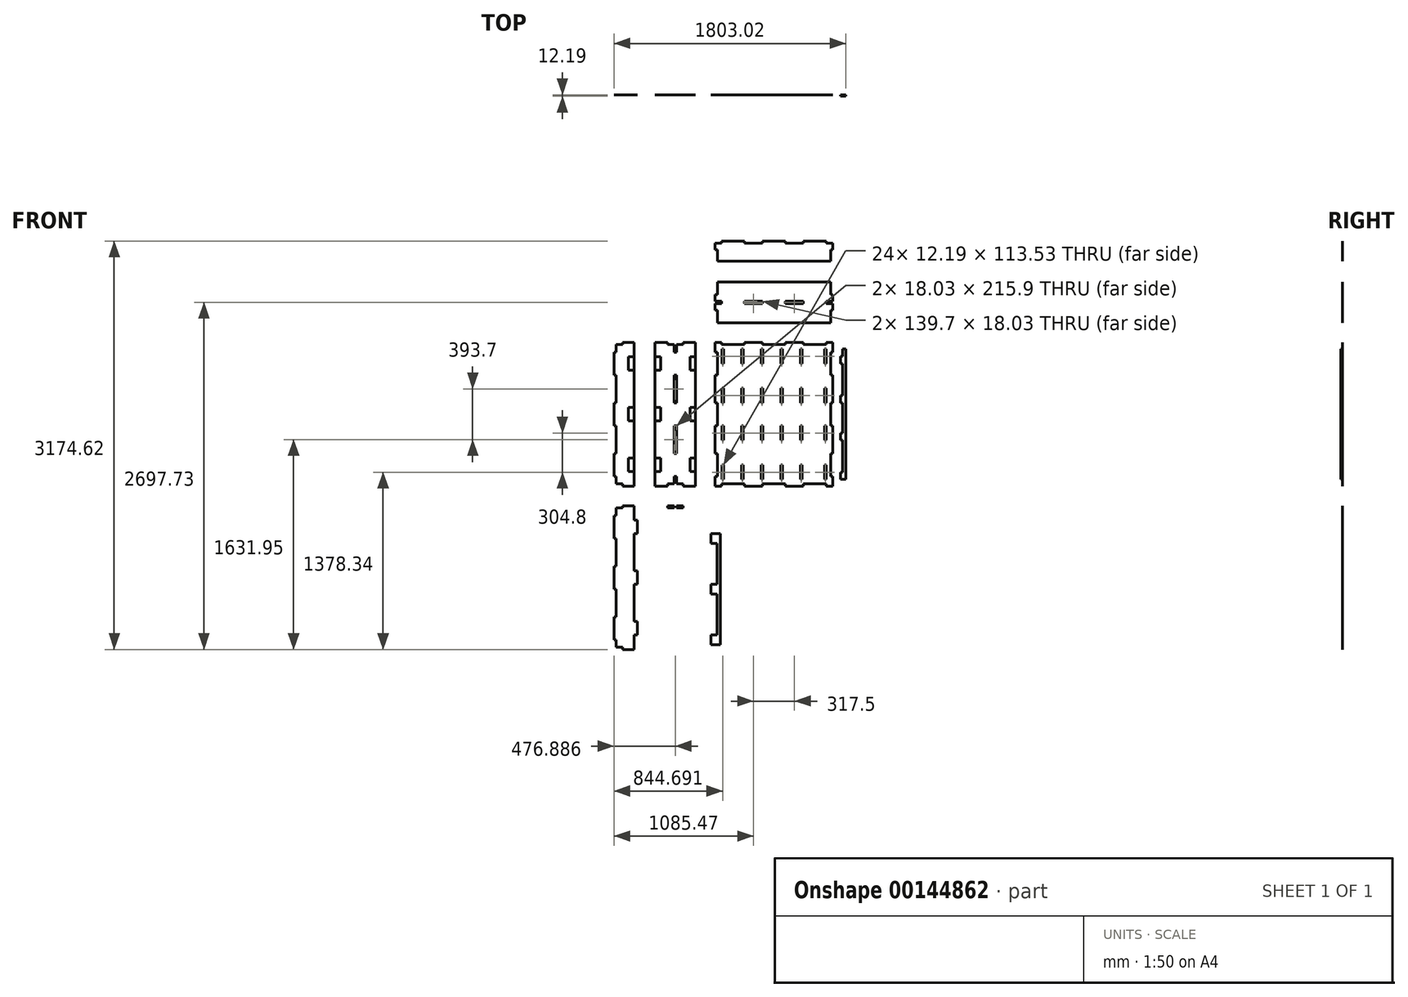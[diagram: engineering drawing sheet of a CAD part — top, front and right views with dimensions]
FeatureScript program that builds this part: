
annotation { "Feature Type Name" : "Feature", "Feature Type Description" : "" }
export const myFeature = defineFeature(function(context is Context, id is Id, definition is map)
    precondition{}
    {
        {
            assignVariable(context, id + "F0", {"name" : "ply34", "anyValue" : 0.71});
        }
        {
            var Q0;
            Q0=qCreatedBy(makeId("Front.planeOp"),FACE);
            var sketch = newSketch(context, id + "F1", { "sketchPlane" : qUnion([Q0])});
            skLineSegment(sketch, "E0.bottom", {"start": v(-457.2, 558.8) * mm, "end": v(457.2, 558.8) * mm});
            skLineSegment(sketch, "E0.top", {"start": v(-457.2, -558.8) * mm, "end": v(457.2, -558.8) * mm});
            skLineSegment(sketch, "E0.left", {"start": v(-457.2, 558.8) * mm, "end": v(-457.2, -558.8) * mm});
            skLineSegment(sketch, "E0.right", {"start": v(457.2, 558.8) * mm, "end": v(457.2, -558.8) * mm});
            skPoint(sketch, "E0.middle", {"position": v(0, 0) * mm});
            skLineSegment(sketch, "E1.bottom", {"start": v(-457.2, 482.6) * mm, "end": v(-439.17, 482.6) * mm});
            skLineSegment(sketch, "E1.top", {"start": v(-457.2, 304.8) * mm, "end": v(-439.17, 304.8) * mm});
            skLineSegment(sketch, "E1.left", {"start": v(-457.2, 482.6) * mm, "end": v(-457.2, 304.8) * mm});
            skLineSegment(sketch, "E1.right", {"start": v(-439.17, 482.6) * mm, "end": v(-439.17, 304.8) * mm});
            skLineSegment(sketch, "E2.bottom", {"start": v(-457.2, 88.9) * mm, "end": v(-439.17, 88.9) * mm});
            skLineSegment(sketch, "E2.top", {"start": v(-457.2, -88.9) * mm, "end": v(-439.17, -88.9) * mm});
            skLineSegment(sketch, "E2.left", {"start": v(-457.2, 88.9) * mm, "end": v(-457.2, -88.9) * mm});
            skLineSegment(sketch, "E2.right", {"start": v(-439.17, 88.9) * mm, "end": v(-439.17, -88.9) * mm});
            skPoint(sketch, "E3", {"position": v(-439.17, 0) * mm});
            skLineSegment(sketch, "E4", {"start": v(-457.2, 0) * mm, "end": v(457.2, 0) * mm, "construction": true});
            skLineSegment(sketch, "E5", {"start": v(0, 558.8) * mm, "end": v(0, -558.8) * mm, "construction": true});
            skLineSegment(sketch, "E6.MirrorCS", {"start": v(-457.2, -482.6) * mm, "end": v(-439.17, -482.6) * mm});
            skLineSegment(sketch, "E7.MirrorCS", {"start": v(-457.2, -304.8) * mm, "end": v(-439.17, -304.8) * mm});
            skLineSegment(sketch, "E8.MirrorCS", {"start": v(-457.2, -482.6) * mm, "end": v(-457.2, -304.8) * mm});
            skLineSegment(sketch, "E9.MirrorCS", {"start": v(-439.17, -482.6) * mm, "end": v(-439.17, -304.8) * mm});
            skLineSegment(sketch, "E10.MirrorCS", {"start": v(457.2, -88.9) * mm, "end": v(439.17, -88.9) * mm});
            skLineSegment(sketch, "E11.MirrorCS", {"start": v(457.2, 304.8) * mm, "end": v(439.17, 304.8) * mm});
            skLineSegment(sketch, "E12.MirrorCS", {"start": v(457.2, 482.6) * mm, "end": v(439.17, 482.6) * mm});
            skLineSegment(sketch, "E13.MirrorCS", {"start": v(457.2, 88.9) * mm, "end": v(439.17, 88.9) * mm});
            skLineSegment(sketch, "E14.MirrorCS", {"start": v(457.2, -304.8) * mm, "end": v(439.17, -304.8) * mm});
            skLineSegment(sketch, "E15.MirrorCS", {"start": v(457.2, -482.6) * mm, "end": v(439.17, -482.6) * mm});
            skLineSegment(sketch, "E16.MirrorCS", {"start": v(439.17, 88.9) * mm, "end": v(439.17, -88.9) * mm});
            skLineSegment(sketch, "E17.MirrorCS", {"start": v(457.2, 88.9) * mm, "end": v(457.2, -88.9) * mm});
            skLineSegment(sketch, "E18.MirrorCS", {"start": v(457.2, -482.6) * mm, "end": v(457.2, -304.8) * mm});
            skLineSegment(sketch, "E19.MirrorCS", {"start": v(439.17, -482.6) * mm, "end": v(439.17, -304.8) * mm});
            skLineSegment(sketch, "E20.MirrorCS", {"start": v(457.2, 482.6) * mm, "end": v(457.2, 304.8) * mm});
            skPoint(sketch, "E21.MirrorP", {"position": v(439.17, 0) * mm});
            skLineSegment(sketch, "E22.MirrorCS", {"start": v(439.17, 482.6) * mm, "end": v(439.17, 304.8) * mm});
            skLineSegment(sketch, "E23.bottom", {"start": v(-406.4, 558.8) * mm, "end": v(-228.6, 558.8) * mm});
            skLineSegment(sketch, "E23.top", {"start": v(-406.4, 540.77) * mm, "end": v(-228.6, 540.77) * mm});
            skLineSegment(sketch, "E23.left", {"start": v(-406.4, 558.8) * mm, "end": v(-406.4, 540.77) * mm});
            skLineSegment(sketch, "E23.right", {"start": v(-228.6, 558.8) * mm, "end": v(-228.6, 540.77) * mm});
            skLineSegment(sketch, "E24.bottom", {"start": v(-88.9, 558.8) * mm, "end": v(88.9, 558.8) * mm});
            skLineSegment(sketch, "E24.top", {"start": v(-88.9, 540.77) * mm, "end": v(88.9, 540.77) * mm});
            skLineSegment(sketch, "E24.left", {"start": v(-88.9, 558.8) * mm, "end": v(-88.9, 540.77) * mm});
            skLineSegment(sketch, "E24.right", {"start": v(88.9, 558.8) * mm, "end": v(88.9, 540.77) * mm});
            skPoint(sketch, "E25", {"position": v(0, 558.8) * mm});
            skLineSegment(sketch, "E26.MirrorCS", {"start": v(228.6, 558.8) * mm, "end": v(228.6, 540.77) * mm});
            skLineSegment(sketch, "E27.MirrorCS", {"start": v(406.4, 558.8) * mm, "end": v(406.4, 540.77) * mm});
            skLineSegment(sketch, "E28.MirrorCS", {"start": v(406.4, 540.77) * mm, "end": v(228.6, 540.77) * mm});
            skLineSegment(sketch, "E29.MirrorCS", {"start": v(406.4, 558.8) * mm, "end": v(228.6, 558.8) * mm});
            skLineSegment(sketch, "E30.MirrorCS", {"start": v(-88.9, -558.8) * mm, "end": v(88.9, -558.8) * mm});
            skLineSegment(sketch, "E31.MirrorCS", {"start": v(228.6, -558.8) * mm, "end": v(228.6, -540.77) * mm});
            skLineSegment(sketch, "E32.MirrorCS", {"start": v(-228.6, -558.8) * mm, "end": v(-228.6, -540.77) * mm});
            skLineSegment(sketch, "E33.MirrorCS", {"start": v(88.9, -558.8) * mm, "end": v(88.9, -540.77) * mm});
            skLineSegment(sketch, "E34.MirrorCS", {"start": v(-406.4, -558.8) * mm, "end": v(-406.4, -540.77) * mm});
            skLineSegment(sketch, "E35.MirrorCS", {"start": v(-88.9, -558.8) * mm, "end": v(-88.9, -540.77) * mm});
            skLineSegment(sketch, "E36.MirrorCS", {"start": v(406.4, -558.8) * mm, "end": v(406.4, -540.77) * mm});
            skLineSegment(sketch, "E37.MirrorCS", {"start": v(-406.4, -558.8) * mm, "end": v(-228.6, -558.8) * mm});
            skLineSegment(sketch, "E38.MirrorCS", {"start": v(-88.9, -540.77) * mm, "end": v(88.9, -540.77) * mm});
            skLineSegment(sketch, "E39.MirrorCS", {"start": v(-406.4, -540.77) * mm, "end": v(-228.6, -540.77) * mm});
            skLineSegment(sketch, "E40.MirrorCS", {"start": v(406.4, -558.8) * mm, "end": v(228.6, -558.8) * mm});
            skLineSegment(sketch, "E41.MirrorCS", {"start": v(406.4, -540.77) * mm, "end": v(228.6, -540.77) * mm});
            skPoint(sketch, "E42.MirrorP", {"position": v(0, -558.8) * mm});
            skLineSegment(sketch, "E43.bottom", {"start": v(-609.6, -558.8) * mm, "end": v(-925.07, -558.8) * mm});
            skLineSegment(sketch, "E43.top", {"start": v(-609.6, 558.8) * mm, "end": v(-925.07, 558.8) * mm});
            skLineSegment(sketch, "E43.left", {"start": v(-609.6, -558.8) * mm, "end": v(-609.6, 558.8) * mm});
            skLineSegment(sketch, "E43.right", {"start": v(-925.07, -558.8) * mm, "end": v(-925.07, 558.8) * mm});
            skLineSegment(sketch, "E44.bottom", {"start": v(-776.35, 558.8) * mm, "end": v(-758.32, 558.8) * mm});
            skLineSegment(sketch, "E44.top", {"start": v(-776.35, 482.6) * mm, "end": v(-758.32, 482.6) * mm});
            skLineSegment(sketch, "E44.left", {"start": v(-776.35, 558.8) * mm, "end": v(-776.35, 482.6) * mm});
            skLineSegment(sketch, "E44.right", {"start": v(-758.32, 558.8) * mm, "end": v(-758.32, 482.6) * mm});
            skPoint(sketch, "E45", {"position": v(-767.33, 558.8) * mm});
            skLineSegment(sketch, "E46.bottom", {"start": v(-776.35, 304.8) * mm, "end": v(-758.32, 304.8) * mm});
            skLineSegment(sketch, "E46.top", {"start": v(-776.35, 88.9) * mm, "end": v(-758.32, 88.9) * mm});
            skLineSegment(sketch, "E46.left", {"start": v(-776.35, 304.8) * mm, "end": v(-776.35, 88.9) * mm});
            skLineSegment(sketch, "E46.right", {"start": v(-758.32, 304.8) * mm, "end": v(-758.32, 88.9) * mm});
            skLineSegment(sketch, "E47.bottom", {"start": v(-776.35, -88.9) * mm, "end": v(-758.32, -88.9) * mm});
            skLineSegment(sketch, "E47.top", {"start": v(-776.35, -304.8) * mm, "end": v(-758.32, -304.8) * mm});
            skLineSegment(sketch, "E47.left", {"start": v(-776.35, -88.9) * mm, "end": v(-776.35, -304.8) * mm});
            skLineSegment(sketch, "E47.right", {"start": v(-758.32, -88.9) * mm, "end": v(-758.32, -304.8) * mm});
            skLineSegment(sketch, "E48.bottom", {"start": v(-776.35, -482.6) * mm, "end": v(-758.32, -482.6) * mm});
            skLineSegment(sketch, "E48.top", {"start": v(-776.35, -558.8) * mm, "end": v(-758.32, -558.8) * mm});
            skLineSegment(sketch, "E48.left", {"start": v(-776.35, -482.6) * mm, "end": v(-776.35, -558.8) * mm});
            skLineSegment(sketch, "E48.right", {"start": v(-758.32, -482.6) * mm, "end": v(-758.32, -558.8) * mm});
            skLineSegment(sketch, "E49.bottom", {"start": v(-776.35, 558.8) * mm, "end": v(-827.15, 558.8) * mm});
            skLineSegment(sketch, "E49.top", {"start": v(-776.35, 540.77) * mm, "end": v(-827.15, 540.77) * mm});
            skLineSegment(sketch, "E49.left", {"start": v(-776.35, 558.8) * mm, "end": v(-776.35, 540.77) * mm});
            skLineSegment(sketch, "E49.right", {"start": v(-827.15, 558.8) * mm, "end": v(-827.15, 540.77) * mm});
            skLineSegment(sketch, "E50.bottom", {"start": v(-758.32, 558.8) * mm, "end": v(-707.52, 558.8) * mm});
            skLineSegment(sketch, "E50.top", {"start": v(-758.32, 540.77) * mm, "end": v(-707.52, 540.77) * mm});
            skLineSegment(sketch, "E50.left", {"start": v(-758.32, 558.8) * mm, "end": v(-758.32, 540.77) * mm});
            skLineSegment(sketch, "E50.right", {"start": v(-707.52, 558.8) * mm, "end": v(-707.52, 540.77) * mm});
            skLineSegment(sketch, "E51.MirrorCS", {"start": v(-758.32, -540.77) * mm, "end": v(-707.52, -540.77) * mm});
            skLineSegment(sketch, "E52.MirrorCS", {"start": v(-758.32, -558.8) * mm, "end": v(-707.52, -558.8) * mm});
            skLineSegment(sketch, "E53.MirrorCS", {"start": v(-758.32, -558.8) * mm, "end": v(-758.32, -540.77) * mm});
            skLineSegment(sketch, "E54.MirrorCS", {"start": v(-827.15, -558.8) * mm, "end": v(-827.15, -540.77) * mm});
            skLineSegment(sketch, "E55.MirrorCS", {"start": v(-776.35, -540.77) * mm, "end": v(-827.15, -540.77) * mm});
            skPoint(sketch, "E56.MirrorP", {"position": v(-767.33, -558.8) * mm});
            skLineSegment(sketch, "E57.MirrorCS", {"start": v(-776.35, -558.8) * mm, "end": v(-776.35, -540.77) * mm});
            skLineSegment(sketch, "E58.MirrorCS", {"start": v(-776.35, -558.8) * mm, "end": v(-827.15, -558.8) * mm});
            skLineSegment(sketch, "E59.MirrorCS", {"start": v(-707.52, -558.8) * mm, "end": v(-707.52, -540.77) * mm});
            skLineSegment(sketch, "E60.bottom", {"start": v(-439.17, 1026.67) * mm, "end": v(439.17, 1026.67) * mm});
            skLineSegment(sketch, "E60.top", {"start": v(-439.17, 711.2) * mm, "end": v(439.17, 711.2) * mm});
            skLineSegment(sketch, "E60.left", {"start": v(-439.17, 1026.67) * mm, "end": v(-439.17, 711.2) * mm});
            skLineSegment(sketch, "E60.right", {"start": v(439.17, 1026.67) * mm, "end": v(439.17, 711.2) * mm});
            skLineSegment(sketch, "E61.bottom", {"start": v(-439.17, 877.95) * mm, "end": v(-457.2, 877.95) * mm});
            skLineSegment(sketch, "E61.top", {"start": v(-439.17, 928.75) * mm, "end": v(-457.2, 928.75) * mm});
            skLineSegment(sketch, "E61.left", {"start": v(-439.17, 877.95) * mm, "end": v(-439.17, 928.75) * mm});
            skLineSegment(sketch, "E61.right", {"start": v(-457.2, 877.95) * mm, "end": v(-457.2, 928.75) * mm});
            skLineSegment(sketch, "E62.bottom", {"start": v(-439.17, 859.92) * mm, "end": v(-457.2, 859.92) * mm});
            skLineSegment(sketch, "E62.top", {"start": v(-439.17, 809.12) * mm, "end": v(-457.2, 809.12) * mm});
            skLineSegment(sketch, "E62.left", {"start": v(-439.17, 859.92) * mm, "end": v(-439.17, 809.12) * mm});
            skLineSegment(sketch, "E62.right", {"start": v(-457.2, 859.92) * mm, "end": v(-457.2, 809.12) * mm});
            skLineSegment(sketch, "E63", {"start": v(-448.18, 877.95) * mm, "end": v(-448.18, 859.92) * mm, "construction": true});
            skPoint(sketch, "E64", {"position": v(-448.18, 868.93) * mm});
            skPoint(sketch, "E65", {"position": v(-439.17, 868.93) * mm});
            skLineSegment(sketch, "E66.bottom", {"start": v(-439.17, 877.95) * mm, "end": v(-406.4, 877.95) * mm});
            skLineSegment(sketch, "E66.top", {"start": v(-439.17, 859.92) * mm, "end": v(-406.4, 859.92) * mm});
            skLineSegment(sketch, "E66.left", {"start": v(-439.17, 877.95) * mm, "end": v(-439.17, 859.92) * mm});
            skLineSegment(sketch, "E66.right", {"start": v(-406.4, 877.95) * mm, "end": v(-406.4, 859.92) * mm});
            skLineSegment(sketch, "E67.bottom", {"start": v(-228.6, 877.95) * mm, "end": v(-88.9, 877.95) * mm});
            skLineSegment(sketch, "E67.top", {"start": v(-228.6, 859.92) * mm, "end": v(-88.9, 859.92) * mm});
            skLineSegment(sketch, "E67.left", {"start": v(-228.6, 877.95) * mm, "end": v(-228.6, 859.92) * mm});
            skLineSegment(sketch, "E67.right", {"start": v(-88.9, 877.95) * mm, "end": v(-88.9, 859.92) * mm});
            skLineSegment(sketch, "E68.bottom", {"start": v(88.9, 877.95) * mm, "end": v(228.6, 877.95) * mm});
            skLineSegment(sketch, "E68.top", {"start": v(88.9, 859.92) * mm, "end": v(228.6, 859.92) * mm});
            skLineSegment(sketch, "E68.left", {"start": v(88.9, 877.95) * mm, "end": v(88.9, 859.92) * mm});
            skLineSegment(sketch, "E68.right", {"start": v(228.6, 877.95) * mm, "end": v(228.6, 859.92) * mm});
            skLineSegment(sketch, "E69.MirrorCS", {"start": v(439.17, 877.95) * mm, "end": v(439.17, 859.92) * mm});
            skLineSegment(sketch, "E70.MirrorCS", {"start": v(439.17, 877.95) * mm, "end": v(457.2, 877.95) * mm});
            skLineSegment(sketch, "E71.MirrorCS", {"start": v(406.4, 877.95) * mm, "end": v(406.4, 859.92) * mm});
            skLineSegment(sketch, "E72.MirrorCS", {"start": v(439.17, 928.75) * mm, "end": v(457.2, 928.75) * mm});
            skLineSegment(sketch, "E73.MirrorCS", {"start": v(448.18, 877.95) * mm, "end": v(448.18, 859.92) * mm, "construction": true});
            skLineSegment(sketch, "E74.MirrorCS", {"start": v(439.17, 809.12) * mm, "end": v(457.2, 809.12) * mm});
            skLineSegment(sketch, "E75.MirrorCS", {"start": v(439.17, 859.92) * mm, "end": v(457.2, 859.92) * mm});
            skLineSegment(sketch, "E76.MirrorCS", {"start": v(439.17, 877.95) * mm, "end": v(406.4, 877.95) * mm});
            skLineSegment(sketch, "E77.MirrorCS", {"start": v(439.17, 859.92) * mm, "end": v(406.4, 859.92) * mm});
            skLineSegment(sketch, "E78.MirrorCS", {"start": v(439.17, 877.95) * mm, "end": v(439.17, 928.75) * mm});
            skLineSegment(sketch, "E79.MirrorCS", {"start": v(439.17, 859.92) * mm, "end": v(439.17, 809.12) * mm});
            skLineSegment(sketch, "E80.MirrorCS", {"start": v(457.2, 877.95) * mm, "end": v(457.2, 928.75) * mm});
            skPoint(sketch, "E81.MirrorP", {"position": v(439.17, 868.93) * mm});
            skLineSegment(sketch, "E82.MirrorCS", {"start": v(457.2, 859.92) * mm, "end": v(457.2, 809.12) * mm});
            skPoint(sketch, "E83.MirrorP", {"position": v(448.18, 868.93) * mm});
            skLineSegment(sketch, "E84", {"start": v(-767.33, -558.8) * mm, "end": v(-767.33, 558.8) * mm, "construction": true});
            skLineSegment(sketch, "E85", {"start": v(439.17, 1102.87) * mm, "end": v(-439.17, 1102.87) * mm, "construction": true});
            skLineSegment(sketch, "E86.MirrorCS", {"start": v(228.6, 1327.78) * mm, "end": v(228.6, 1345.82) * mm});
            skLineSegment(sketch, "E87.MirrorCS", {"start": v(-228.6, 1327.78) * mm, "end": v(-228.6, 1345.82) * mm});
            skLineSegment(sketch, "E88.MirrorCS", {"start": v(-88.9, 1327.78) * mm, "end": v(-88.9, 1345.82) * mm});
            skLineSegment(sketch, "E89.MirrorCS", {"start": v(88.9, 1327.78) * mm, "end": v(88.9, 1345.82) * mm});
            skLineSegment(sketch, "E90.MirrorCS", {"start": v(-228.6, 1345.82) * mm, "end": v(-88.9, 1345.82) * mm});
            skLineSegment(sketch, "E91.MirrorCS", {"start": v(-228.6, 1327.78) * mm, "end": v(-88.9, 1327.78) * mm});
            skLineSegment(sketch, "E92.MirrorCS", {"start": v(88.9, 1345.82) * mm, "end": v(228.6, 1345.82) * mm});
            skLineSegment(sketch, "E93.MirrorCS", {"start": v(88.9, 1327.78) * mm, "end": v(228.6, 1327.78) * mm});
            skLineSegment(sketch, "E94.MirrorCS", {"start": v(439.17, 1276.98) * mm, "end": v(457.2, 1276.98) * mm});
            skLineSegment(sketch, "E95.MirrorCS", {"start": v(457.2, 1327.78) * mm, "end": v(457.2, 1276.98) * mm});
            skLineSegment(sketch, "E96.MirrorCS", {"start": v(439.17, 1327.78) * mm, "end": v(457.2, 1327.78) * mm});
            skLineSegment(sketch, "E97.MirrorCS", {"start": v(439.17, 1327.78) * mm, "end": v(406.4, 1327.78) * mm});
            skLineSegment(sketch, "E98.MirrorCS", {"start": v(406.4, 1327.78) * mm, "end": v(406.4, 1345.82) * mm});
            skLineSegment(sketch, "E99.MirrorCS", {"start": v(439.17, 1345.82) * mm, "end": v(406.4, 1345.82) * mm});
            skLineSegment(sketch, "E100.MirrorCS", {"start": v(-439.17, 1276.98) * mm, "end": v(-457.2, 1276.98) * mm});
            skLineSegment(sketch, "E101.MirrorCS", {"start": v(-457.2, 1327.78) * mm, "end": v(-457.2, 1276.98) * mm});
            skLineSegment(sketch, "E102.MirrorCS", {"start": v(-439.17, 1327.78) * mm, "end": v(-457.2, 1327.78) * mm});
            skLineSegment(sketch, "E103.MirrorCS", {"start": v(-439.17, 1327.78) * mm, "end": v(-406.4, 1327.78) * mm});
            skLineSegment(sketch, "E104.MirrorCS", {"start": v(-406.4, 1327.78) * mm, "end": v(-406.4, 1345.82) * mm});
            skLineSegment(sketch, "E105.MirrorCS", {"start": v(-439.17, 1345.82) * mm, "end": v(-406.4, 1345.82) * mm});
            skLineSegment(sketch, "E106", {"start": v(-406.4, 1345.82) * mm, "end": v(-228.6, 1345.82) * mm});
            skLineSegment(sketch, "E107", {"start": v(-88.9, 1345.82) * mm, "end": v(88.9, 1345.82) * mm});
            skLineSegment(sketch, "E108", {"start": v(228.6, 1345.82) * mm, "end": v(406.4, 1345.82) * mm});
            skLineSegment(sketch, "E109.bottom", {"start": v(-609.6, 52.07) * mm, "end": v(-653.31, 52.07) * mm});
            skLineSegment(sketch, "E109.top", {"start": v(-609.6, -52.07) * mm, "end": v(-653.31, -52.07) * mm});
            skLineSegment(sketch, "E109.left", {"start": v(-609.6, 52.07) * mm, "end": v(-609.6, -52.07) * mm});
            skLineSegment(sketch, "E109.right", {"start": v(-653.31, 52.07) * mm, "end": v(-653.31, -52.07) * mm});
            skPoint(sketch, "E110", {"position": v(-609.6, 0) * mm});
            skLineSegment(sketch, "E111", {"start": v(-758.32, 482.6) * mm, "end": v(-758.32, 304.8) * mm, "construction": true});
            skLineSegment(sketch, "E112.bottom", {"start": v(-653.31, 341.63) * mm, "end": v(-609.6, 341.63) * mm});
            skLineSegment(sketch, "E112.top", {"start": v(-653.31, 445.77) * mm, "end": v(-609.6, 445.77) * mm});
            skLineSegment(sketch, "E112.left", {"start": v(-653.31, 341.63) * mm, "end": v(-653.31, 445.77) * mm});
            skLineSegment(sketch, "E112.right", {"start": v(-609.6, 341.63) * mm, "end": v(-609.6, 445.77) * mm});
            skPoint(sketch, "E112.middle", {"position": v(-631.46, 393.7) * mm});
            skPoint(sketch, "E112.middle.positionSnap0", {"position": v(-631.46, 52.07) * mm});
            skPoint(sketch, "E112.middle.positionSnap1", {"position": v(-758.32, 393.7) * mm});
            skPoint(sketch, "E112.centerSnap0", {"position": v(-631.46, 52.07) * mm});
            skPoint(sketch, "E112.centerSnap1", {"position": v(-758.32, 393.7) * mm});
            skLineSegment(sketch, "E113.MirrorCS", {"start": v(-653.31, -341.63) * mm, "end": v(-609.6, -341.63) * mm});
            skLineSegment(sketch, "E114.MirrorCS", {"start": v(-653.31, -445.77) * mm, "end": v(-609.6, -445.77) * mm});
            skLineSegment(sketch, "E115.MirrorCS", {"start": v(-653.31, -341.63) * mm, "end": v(-653.31, -445.77) * mm});
            skPoint(sketch, "E116.MirrorP", {"position": v(-631.46, -393.7) * mm});
            skLineSegment(sketch, "E117.MirrorCS", {"start": v(-609.6, -341.63) * mm, "end": v(-609.6, -445.77) * mm});
            skLineSegment(sketch, "E118.MirrorCS", {"start": v(-881.35, -445.77) * mm, "end": v(-925.07, -445.77) * mm});
            skLineSegment(sketch, "E119.MirrorCS", {"start": v(-881.35, -341.63) * mm, "end": v(-925.07, -341.63) * mm});
            skLineSegment(sketch, "E120.MirrorCS", {"start": v(-881.35, 445.77) * mm, "end": v(-925.07, 445.77) * mm});
            skLineSegment(sketch, "E121.MirrorCS", {"start": v(-881.35, 341.63) * mm, "end": v(-925.07, 341.63) * mm});
            skLineSegment(sketch, "E122.MirrorCS", {"start": v(-925.07, -52.07) * mm, "end": v(-881.35, -52.07) * mm});
            skLineSegment(sketch, "E123.MirrorCS", {"start": v(-925.07, 52.07) * mm, "end": v(-881.35, 52.07) * mm});
            skLineSegment(sketch, "E124.MirrorCS", {"start": v(-925.07, -341.63) * mm, "end": v(-925.07, -445.77) * mm});
            skPoint(sketch, "E125.MirrorP", {"position": v(-903.21, 52.07) * mm});
            skLineSegment(sketch, "E126.MirrorCS", {"start": v(-881.35, -341.63) * mm, "end": v(-881.35, -445.77) * mm});
            skLineSegment(sketch, "E127.MirrorCS", {"start": v(-925.07, 341.63) * mm, "end": v(-925.07, 445.77) * mm});
            skLineSegment(sketch, "E128.MirrorCS", {"start": v(-881.35, 341.63) * mm, "end": v(-881.35, 445.77) * mm});
            skLineSegment(sketch, "E129.MirrorCS", {"start": v(-925.07, 52.07) * mm, "end": v(-925.07, -52.07) * mm});
            skLineSegment(sketch, "E130.MirrorCS", {"start": v(-881.35, 52.07) * mm, "end": v(-881.35, -52.07) * mm});
            skPoint(sketch, "E131.MirrorP", {"position": v(-903.21, 393.7) * mm});
            skPoint(sketch, "E132.MirrorP", {"position": v(-925.07, 0) * mm});
            skPoint(sketch, "E133.MirrorP", {"position": v(-903.21, -393.7) * mm});
            skLineSegment(sketch, "E134.bottom", {"start": v(-405.63, 507.23) * mm, "end": v(405.63, 507.23) * mm, "construction": true});
            skLineSegment(sketch, "E134.top", {"start": v(-405.63, -507.23) * mm, "end": v(405.63, -507.23) * mm, "construction": true});
            skLineSegment(sketch, "E134.left", {"start": v(-405.63, 507.23) * mm, "end": v(-405.63, -507.23) * mm, "construction": true});
            skLineSegment(sketch, "E134.right", {"start": v(405.63, 507.23) * mm, "end": v(405.63, -507.23) * mm, "construction": true});
            skLineSegment(sketch, "E135.0", {"start": v(-393.43, 495.03) * mm, "end": v(393.43, 495.03) * mm, "construction": true});
            skLineSegment(sketch, "E135.1", {"start": v(-393.43, 495.03) * mm, "end": v(-393.43, -495.03) * mm, "construction": true});
            skLineSegment(sketch, "E135.2", {"start": v(-393.43, -495.03) * mm, "end": v(393.43, -495.03) * mm, "construction": true});
            skLineSegment(sketch, "E135.3", {"start": v(393.43, 495.03) * mm, "end": v(393.43, -495.03) * mm, "construction": true});
            skPoint(sketch, "E136.oppositeSnap0", {"position": v(-439.17, 393.7) * mm});
            skLineSegment(sketch, "E136.bottom", {"start": v(-405.63, 507.23) * mm, "end": v(-393.43, 507.23) * mm});
            skLineSegment(sketch, "E136.top", {"start": v(-405.63, 393.7) * mm, "end": v(-393.43, 393.7) * mm});
            skLineSegment(sketch, "E136.left", {"start": v(-405.63, 507.23) * mm, "end": v(-405.63, 393.7) * mm});
            skLineSegment(sketch, "E136.right", {"start": v(-393.43, 507.23) * mm, "end": v(-393.43, 393.7) * mm});
            skPoint(sketch, "E137.oppositeSnap0", {"position": v(-439.17, -393.7) * mm});
            skLineSegment(sketch, "E137.bottom", {"start": v(-405.63, -507.23) * mm, "end": v(-393.43, -507.23) * mm});
            skLineSegment(sketch, "E137.top", {"start": v(-405.63, -393.7) * mm, "end": v(-393.43, -393.7) * mm});
            skLineSegment(sketch, "E137.left", {"start": v(-405.63, -507.23) * mm, "end": v(-405.63, -393.7) * mm});
            skLineSegment(sketch, "E137.right", {"start": v(-393.43, -507.23) * mm, "end": v(-393.43, -393.7) * mm});
            skLineSegment(sketch, "E138.bottom", {"start": v(-405.63, 88.9) * mm, "end": v(-393.43, 88.9) * mm});
            skLineSegment(sketch, "E138.top", {"start": v(-405.63, 202.43) * mm, "end": v(-393.43, 202.43) * mm});
            skLineSegment(sketch, "E138.left", {"start": v(-405.63, 88.9) * mm, "end": v(-405.63, 202.43) * mm});
            skLineSegment(sketch, "E138.right", {"start": v(-393.43, 88.9) * mm, "end": v(-393.43, 202.43) * mm});
            skLineSegment(sketch, "E139.bottom", {"start": v(-405.63, -88.9) * mm, "end": v(-393.43, -88.9) * mm});
            skLineSegment(sketch, "E139.top", {"start": v(-405.63, -202.43) * mm, "end": v(-393.43, -202.43) * mm});
            skLineSegment(sketch, "E139.left", {"start": v(-405.63, -88.9) * mm, "end": v(-405.63, -202.43) * mm});
            skLineSegment(sketch, "E139.right", {"start": v(-393.43, -88.9) * mm, "end": v(-393.43, -202.43) * mm});
            skLineSegment(sketch, "E140.1.0.0", {"start": v(-253.23, -507.23) * mm, "end": v(-253.23, -393.7) * mm});
            skLineSegment(sketch, "E140.1.0.1", {"start": v(-241.03, -507.23) * mm, "end": v(-241.03, -393.7) * mm});
            skLineSegment(sketch, "E140.1.0.2", {"start": v(-253.23, -507.23) * mm, "end": v(-241.03, -507.23) * mm});
            skLineSegment(sketch, "E140.1.0.3", {"start": v(-253.23, -393.7) * mm, "end": v(-241.03, -393.7) * mm});
            skLineSegment(sketch, "E140.1.0.4", {"start": v(-253.23, -88.9) * mm, "end": v(-241.03, -88.9) * mm});
            skLineSegment(sketch, "E140.1.0.5", {"start": v(-253.23, -202.43) * mm, "end": v(-241.03, -202.43) * mm});
            skLineSegment(sketch, "E140.1.0.6", {"start": v(-253.23, -88.9) * mm, "end": v(-253.23, -202.43) * mm});
            skLineSegment(sketch, "E140.1.0.7", {"start": v(-241.03, -88.9) * mm, "end": v(-241.03, -202.43) * mm});
            skLineSegment(sketch, "E140.1.0.8", {"start": v(-253.23, 88.9) * mm, "end": v(-253.23, 202.43) * mm});
            skLineSegment(sketch, "E140.1.0.9", {"start": v(-241.03, 88.9) * mm, "end": v(-241.03, 202.43) * mm});
            skLineSegment(sketch, "E140.1.0.10", {"start": v(-253.23, 88.9) * mm, "end": v(-241.03, 88.9) * mm});
            skLineSegment(sketch, "E140.1.0.11", {"start": v(-253.23, 202.43) * mm, "end": v(-241.03, 202.43) * mm});
            skLineSegment(sketch, "E140.1.0.12", {"start": v(-253.23, 507.23) * mm, "end": v(-241.03, 507.23) * mm});
            skLineSegment(sketch, "E140.1.0.13", {"start": v(-253.23, 393.7) * mm, "end": v(-241.03, 393.7) * mm});
            skLineSegment(sketch, "E140.1.0.14", {"start": v(-253.23, 507.23) * mm, "end": v(-253.23, 393.7) * mm});
            skLineSegment(sketch, "E140.1.0.15", {"start": v(-241.03, 507.23) * mm, "end": v(-241.03, 393.7) * mm});
            skLineSegment(sketch, "E140.2.0.0", {"start": v(-100.83, -507.23) * mm, "end": v(-100.83, -393.7) * mm});
            skLineSegment(sketch, "E140.2.0.1", {"start": v(-88.63, -507.23) * mm, "end": v(-88.63, -393.7) * mm});
            skLineSegment(sketch, "E140.2.0.2", {"start": v(-100.83, -507.23) * mm, "end": v(-88.63, -507.23) * mm});
            skLineSegment(sketch, "E140.2.0.3", {"start": v(-100.83, -393.7) * mm, "end": v(-88.63, -393.7) * mm});
            skLineSegment(sketch, "E140.2.0.4", {"start": v(-100.83, -88.9) * mm, "end": v(-88.63, -88.9) * mm});
            skLineSegment(sketch, "E140.2.0.5", {"start": v(-100.83, -202.43) * mm, "end": v(-88.63, -202.43) * mm});
            skLineSegment(sketch, "E140.2.0.6", {"start": v(-100.83, -88.9) * mm, "end": v(-100.83, -202.43) * mm});
            skLineSegment(sketch, "E140.2.0.7", {"start": v(-88.63, -88.9) * mm, "end": v(-88.63, -202.43) * mm});
            skLineSegment(sketch, "E140.2.0.8", {"start": v(-100.83, 88.9) * mm, "end": v(-100.83, 202.43) * mm});
            skLineSegment(sketch, "E140.2.0.9", {"start": v(-88.63, 88.9) * mm, "end": v(-88.63, 202.43) * mm});
            skLineSegment(sketch, "E140.2.0.10", {"start": v(-100.83, 88.9) * mm, "end": v(-88.63, 88.9) * mm});
            skLineSegment(sketch, "E140.2.0.11", {"start": v(-100.83, 202.43) * mm, "end": v(-88.63, 202.43) * mm});
            skLineSegment(sketch, "E140.2.0.12", {"start": v(-100.83, 507.23) * mm, "end": v(-88.63, 507.23) * mm});
            skLineSegment(sketch, "E140.2.0.13", {"start": v(-100.83, 393.7) * mm, "end": v(-88.63, 393.7) * mm});
            skLineSegment(sketch, "E140.2.0.14", {"start": v(-100.83, 507.23) * mm, "end": v(-100.83, 393.7) * mm});
            skLineSegment(sketch, "E140.2.0.15", {"start": v(-88.63, 507.23) * mm, "end": v(-88.63, 393.7) * mm});
            skLineSegment(sketch, "E140.3.0.0", {"start": v(51.57, -507.23) * mm, "end": v(51.57, -393.7) * mm});
            skLineSegment(sketch, "E140.3.0.1", {"start": v(63.77, -507.23) * mm, "end": v(63.77, -393.7) * mm});
            skLineSegment(sketch, "E140.3.0.2", {"start": v(51.57, -507.23) * mm, "end": v(63.77, -507.23) * mm});
            skLineSegment(sketch, "E140.3.0.3", {"start": v(51.57, -393.7) * mm, "end": v(63.77, -393.7) * mm});
            skLineSegment(sketch, "E140.3.0.4", {"start": v(51.57, -88.9) * mm, "end": v(63.77, -88.9) * mm});
            skLineSegment(sketch, "E140.3.0.5", {"start": v(51.57, -202.43) * mm, "end": v(63.77, -202.43) * mm});
            skLineSegment(sketch, "E140.3.0.6", {"start": v(51.57, -88.9) * mm, "end": v(51.57, -202.43) * mm});
            skLineSegment(sketch, "E140.3.0.7", {"start": v(63.77, -88.9) * mm, "end": v(63.77, -202.43) * mm});
            skLineSegment(sketch, "E140.3.0.8", {"start": v(51.57, 88.9) * mm, "end": v(51.57, 202.43) * mm});
            skLineSegment(sketch, "E140.3.0.9", {"start": v(63.77, 88.9) * mm, "end": v(63.77, 202.43) * mm});
            skLineSegment(sketch, "E140.3.0.10", {"start": v(51.57, 88.9) * mm, "end": v(63.77, 88.9) * mm});
            skLineSegment(sketch, "E140.3.0.11", {"start": v(51.57, 202.43) * mm, "end": v(63.77, 202.43) * mm});
            skLineSegment(sketch, "E140.3.0.12", {"start": v(51.57, 507.23) * mm, "end": v(63.77, 507.23) * mm});
            skLineSegment(sketch, "E140.3.0.13", {"start": v(51.57, 393.7) * mm, "end": v(63.77, 393.7) * mm});
            skLineSegment(sketch, "E140.3.0.14", {"start": v(51.57, 507.23) * mm, "end": v(51.57, 393.7) * mm});
            skLineSegment(sketch, "E140.3.0.15", {"start": v(63.77, 507.23) * mm, "end": v(63.77, 393.7) * mm});
            skLineSegment(sketch, "E140.4.0.0", {"start": v(203.97, -507.23) * mm, "end": v(203.97, -393.7) * mm});
            skLineSegment(sketch, "E140.4.0.1", {"start": v(216.17, -507.23) * mm, "end": v(216.17, -393.7) * mm});
            skLineSegment(sketch, "E140.4.0.2", {"start": v(203.97, -507.23) * mm, "end": v(216.17, -507.23) * mm});
            skLineSegment(sketch, "E140.4.0.3", {"start": v(203.97, -393.7) * mm, "end": v(216.17, -393.7) * mm});
            skLineSegment(sketch, "E140.4.0.4", {"start": v(203.97, -88.9) * mm, "end": v(216.17, -88.9) * mm});
            skLineSegment(sketch, "E140.4.0.5", {"start": v(203.97, -202.43) * mm, "end": v(216.17, -202.43) * mm});
            skLineSegment(sketch, "E140.4.0.6", {"start": v(203.97, -88.9) * mm, "end": v(203.97, -202.43) * mm});
            skLineSegment(sketch, "E140.4.0.7", {"start": v(216.17, -88.9) * mm, "end": v(216.17, -202.43) * mm});
            skLineSegment(sketch, "E140.4.0.8", {"start": v(203.97, 88.9) * mm, "end": v(203.97, 202.43) * mm});
            skLineSegment(sketch, "E140.4.0.9", {"start": v(216.17, 88.9) * mm, "end": v(216.17, 202.43) * mm});
            skLineSegment(sketch, "E140.4.0.10", {"start": v(203.97, 88.9) * mm, "end": v(216.17, 88.9) * mm});
            skLineSegment(sketch, "E140.4.0.11", {"start": v(203.97, 202.43) * mm, "end": v(216.17, 202.43) * mm});
            skLineSegment(sketch, "E140.4.0.12", {"start": v(203.97, 507.23) * mm, "end": v(216.17, 507.23) * mm});
            skLineSegment(sketch, "E140.4.0.13", {"start": v(203.97, 393.7) * mm, "end": v(216.17, 393.7) * mm});
            skLineSegment(sketch, "E140.4.0.14", {"start": v(203.97, 507.23) * mm, "end": v(203.97, 393.7) * mm});
            skLineSegment(sketch, "E140.4.0.15", {"start": v(216.17, 507.23) * mm, "end": v(216.17, 393.7) * mm});
            skLineSegment(sketch, "E140.direction1", {"start": v(-405.63, -507.23) * mm, "end": v(-253.23, -507.23) * mm, "construction": true});
            skLineSegment(sketch, "E141.MirrorCS", {"start": v(405.63, 507.23) * mm, "end": v(393.43, 507.23) * mm});
            skLineSegment(sketch, "E142.MirrorCS", {"start": v(405.63, 393.7) * mm, "end": v(393.43, 393.7) * mm});
            skLineSegment(sketch, "E143.MirrorCS", {"start": v(405.63, 507.23) * mm, "end": v(405.63, 393.7) * mm});
            skLineSegment(sketch, "E144.MirrorCS", {"start": v(393.43, 507.23) * mm, "end": v(393.43, 393.7) * mm});
            skLineSegment(sketch, "E145.MirrorCS", {"start": v(405.63, -202.43) * mm, "end": v(393.43, -202.43) * mm});
            skLineSegment(sketch, "E146.MirrorCS", {"start": v(405.63, -88.9) * mm, "end": v(393.43, -88.9) * mm});
            skLineSegment(sketch, "E147.MirrorCS", {"start": v(405.63, 88.9) * mm, "end": v(393.43, 88.9) * mm});
            skLineSegment(sketch, "E148.MirrorCS", {"start": v(405.63, 202.43) * mm, "end": v(393.43, 202.43) * mm});
            skLineSegment(sketch, "E149.MirrorCS", {"start": v(393.43, 88.9) * mm, "end": v(393.43, 202.43) * mm});
            skLineSegment(sketch, "E150.MirrorCS", {"start": v(393.43, -88.9) * mm, "end": v(393.43, -202.43) * mm});
            skLineSegment(sketch, "E151.MirrorCS", {"start": v(405.63, -88.9) * mm, "end": v(405.63, -202.43) * mm});
            skLineSegment(sketch, "E152.MirrorCS", {"start": v(405.63, 88.9) * mm, "end": v(405.63, 202.43) * mm});
            skLineSegment(sketch, "E153.MirrorCS", {"start": v(393.43, -507.23) * mm, "end": v(393.43, -393.7) * mm});
            skLineSegment(sketch, "E154.MirrorCS", {"start": v(405.63, -507.23) * mm, "end": v(405.63, -393.7) * mm});
            skLineSegment(sketch, "E155.MirrorCS", {"start": v(405.63, -507.23) * mm, "end": v(393.43, -507.23) * mm});
            skLineSegment(sketch, "E156.MirrorCS", {"start": v(405.63, -393.7) * mm, "end": v(393.43, -393.7) * mm});
            skLineSegment(sketch, "E157.bottom", {"start": v(533.4, 507.23) * mm, "end": v(558.8, 507.23) * mm});
            skLineSegment(sketch, "E157.top", {"start": v(533.4, -507.23) * mm, "end": v(558.8, -507.23) * mm});
            skLineSegment(sketch, "E157.left", {"start": v(533.4, 507.23) * mm, "end": v(533.4, -507.23) * mm});
            skLineSegment(sketch, "E157.right", {"start": v(558.8, 507.23) * mm, "end": v(558.8, -507.23) * mm});
            skPoint(sketch, "E158.startSnap0", {"position": v(405.63, 450.46) * mm});
            skPoint(sketch, "E159.endSnap0", {"position": v(533.4, 0) * mm});
            skLineSegment(sketch, "E160", {"start": v(533.4, 88.9) * mm, "end": v(515.37, 88.9) * mm});
            skLineSegment(sketch, "E161", {"start": v(515.37, 88.9) * mm, "end": v(515.37, 145.66) * mm});
            skPoint(sketch, "E161.endSnap0", {"position": v(405.63, 145.66) * mm});
            skLineSegment(sketch, "E162", {"start": v(533.4, 145.66) * mm, "end": v(515.37, 145.66) * mm});
            skLineSegment(sketch, "E163", {"start": v(533.4, 393.7) * mm, "end": v(515.37, 393.7) * mm});
            skPoint(sketch, "E163.startSnap0", {"position": v(457.2, 393.7) * mm});
            skLineSegment(sketch, "E164", {"start": v(515.37, 393.7) * mm, "end": v(515.37, 450.46) * mm});
            skLineSegment(sketch, "E165", {"start": v(533.4, 450.46) * mm, "end": v(515.37, 450.46) * mm});
            skLineSegment(sketch, "E166", {"start": v(533.4, -202.43) * mm, "end": v(515.37, -202.43) * mm});
            skLineSegment(sketch, "E167", {"start": v(515.37, -202.43) * mm, "end": v(515.37, -145.66) * mm});
            skPoint(sketch, "E167.endSnap0", {"position": v(405.63, -145.66) * mm});
            skLineSegment(sketch, "E168", {"start": v(533.4, -145.66) * mm, "end": v(515.37, -145.66) * mm});
            skLineSegment(sketch, "E169", {"start": v(533.4, -507.23) * mm, "end": v(515.37, -507.23) * mm});
            skLineSegment(sketch, "E170", {"start": v(515.37, -507.23) * mm, "end": v(515.37, -450.46) * mm});
            skPoint(sketch, "E171", {"position": v(405.63, -450.46) * mm});
            skLineSegment(sketch, "E172", {"start": v(533.4, -450.46) * mm, "end": v(515.37, -450.46) * mm});
            skLineSegment(sketch, "E173.bottom", {"start": v(-940.94, -711.2) * mm, "end": v(-593.72, -711.2) * mm});
            skLineSegment(sketch, "E173.top", {"start": v(-940.94, -1828.8) * mm, "end": v(-593.72, -1828.8) * mm});
            skLineSegment(sketch, "E173.left", {"start": v(-940.94, -711.2) * mm, "end": v(-940.94, -1828.8) * mm});
            skLineSegment(sketch, "E173.right", {"start": v(-593.72, -711.2) * mm, "end": v(-593.72, -1828.8) * mm});
            skPoint(sketch, "E174", {"position": v(-767.33, -711.2) * mm});
            skLineSegment(sketch, "E175", {"start": v(-925.07, -635) * mm, "end": v(-703.26, -635) * mm, "construction": true});
            skLineSegment(sketch, "E176.MirrorCS", {"start": v(-881.35, -1715.77) * mm, "end": v(-925.07, -1715.77) * mm, "construction": true});
            skLineSegment(sketch, "E177.MirrorCS", {"start": v(-881.35, -1611.63) * mm, "end": v(-925.07, -1611.63) * mm, "construction": true});
            skLineSegment(sketch, "E178.MirrorCS", {"start": v(-653.31, -1611.63) * mm, "end": v(-609.6, -1611.63) * mm, "construction": true});
            skLineSegment(sketch, "E179.MirrorCS", {"start": v(-653.31, -1715.77) * mm, "end": v(-609.6, -1715.77) * mm, "construction": true});
            skLineSegment(sketch, "E180.MirrorCS", {"start": v(-609.6, -1322.07) * mm, "end": v(-653.31, -1322.07) * mm, "construction": true});
            skLineSegment(sketch, "E181.MirrorCS", {"start": v(-925.07, -1322.07) * mm, "end": v(-881.35, -1322.07) * mm, "construction": true});
            skLineSegment(sketch, "E182.MirrorCS", {"start": v(-925.07, -1217.93) * mm, "end": v(-881.35, -1217.93) * mm, "construction": true});
            skLineSegment(sketch, "E183.MirrorCS", {"start": v(-609.6, -1217.93) * mm, "end": v(-653.31, -1217.93) * mm, "construction": true});
            skLineSegment(sketch, "E184.MirrorCS", {"start": v(-881.35, -928.37) * mm, "end": v(-925.07, -928.37) * mm, "construction": true});
            skLineSegment(sketch, "E185.MirrorCS", {"start": v(-881.35, -824.23) * mm, "end": v(-925.07, -824.23) * mm, "construction": true});
            skLineSegment(sketch, "E186.MirrorCS", {"start": v(-653.31, -928.37) * mm, "end": v(-609.6, -928.37) * mm, "construction": true});
            skLineSegment(sketch, "E187.MirrorCS", {"start": v(-653.31, -824.23) * mm, "end": v(-609.6, -824.23) * mm, "construction": true});
            skPoint(sketch, "E188.endSnap0", {"position": v(-903.21, -1322.07) * mm});
            skLineSegment(sketch, "E189.bottom", {"start": v(-940.94, -824.23) * mm, "end": v(-915.54, -824.23) * mm});
            skLineSegment(sketch, "E189.top", {"start": v(-940.94, -928.37) * mm, "end": v(-915.54, -928.37) * mm});
            skLineSegment(sketch, "E189.left", {"start": v(-940.94, -824.23) * mm, "end": v(-940.94, -928.37) * mm});
            skLineSegment(sketch, "E189.right", {"start": v(-915.54, -824.23) * mm, "end": v(-915.54, -928.37) * mm});
            skLineSegment(sketch, "E190.bottom", {"start": v(-940.94, -1004.57) * mm, "end": v(-922.9, -1004.57) * mm});
            skLineSegment(sketch, "E190.top", {"start": v(-940.94, -928.37) * mm, "end": v(-922.9, -928.37) * mm});
            skLineSegment(sketch, "E190.left", {"start": v(-940.94, -1004.57) * mm, "end": v(-940.94, -928.37) * mm});
            skLineSegment(sketch, "E190.right", {"start": v(-922.9, -1004.57) * mm, "end": v(-922.9, -928.37) * mm});
            skLineSegment(sketch, "E191", {"start": v(-940.94, -1270) * mm, "end": v(-593.72, -1270) * mm, "construction": true});
            skLineSegment(sketch, "E192", {"start": v(-767.33, -711.2) * mm, "end": v(-767.33, -1828.8) * mm, "construction": true});
            skLineSegment(sketch, "E193.MirrorCS", {"start": v(-593.73, -928.37) * mm, "end": v(-619.12, -928.37) * mm});
            skLineSegment(sketch, "E194.MirrorCS", {"start": v(-593.73, -928.37) * mm, "end": v(-611.76, -928.37) * mm});
            skLineSegment(sketch, "E195.MirrorCS", {"start": v(-593.73, -1004.57) * mm, "end": v(-611.76, -1004.57) * mm});
            skLineSegment(sketch, "E196.MirrorCS", {"start": v(-593.72, -824.23) * mm, "end": v(-619.12, -824.23) * mm});
            skLineSegment(sketch, "E197.MirrorCS", {"start": v(-611.76, -1004.57) * mm, "end": v(-611.76, -928.37) * mm});
            skLineSegment(sketch, "E198.MirrorCS", {"start": v(-593.72, -1004.57) * mm, "end": v(-593.72, -928.37) * mm});
            skLineSegment(sketch, "E199.MirrorCS", {"start": v(-593.72, -824.23) * mm, "end": v(-593.72, -928.37) * mm});
            skLineSegment(sketch, "E200.MirrorCS", {"start": v(-619.12, -824.23) * mm, "end": v(-619.12, -928.37) * mm});
            skLineSegment(sketch, "E201.MirrorCS", {"start": v(-940.94, -1611.63) * mm, "end": v(-915.54, -1611.63) * mm});
            skLineSegment(sketch, "E202.MirrorCS", {"start": v(-940.94, -1715.77) * mm, "end": v(-915.54, -1715.77) * mm});
            skLineSegment(sketch, "E203.MirrorCS", {"start": v(-940.94, -1715.77) * mm, "end": v(-940.94, -1611.63) * mm});
            skLineSegment(sketch, "E204.MirrorCS", {"start": v(-915.54, -1715.77) * mm, "end": v(-915.54, -1611.63) * mm});
            skLineSegment(sketch, "E205.MirrorCS", {"start": v(-593.73, -1611.63) * mm, "end": v(-619.12, -1611.63) * mm});
            skLineSegment(sketch, "E206.MirrorCS", {"start": v(-593.72, -1715.77) * mm, "end": v(-593.72, -1611.63) * mm});
            skLineSegment(sketch, "E207.MirrorCS", {"start": v(-619.12, -1715.77) * mm, "end": v(-619.12, -1611.63) * mm});
            skLineSegment(sketch, "E208.MirrorCS", {"start": v(-593.72, -1715.77) * mm, "end": v(-619.12, -1715.77) * mm});
            skLineSegment(sketch, "E209", {"start": v(-903.21, -1322.07) * mm, "end": v(-903.21, -1611.63) * mm, "construction": true});
            skLineSegment(sketch, "E210", {"start": v(-903.21, -1466.85) * mm, "end": v(-767.33, -1466.85) * mm, "construction": true});
            skLineSegment(sketch, "E211.MirrorCS", {"start": v(-940.94, -1322.07) * mm, "end": v(-915.54, -1322.07) * mm});
            skLineSegment(sketch, "E212.MirrorCS", {"start": v(-940.94, -1217.93) * mm, "end": v(-915.54, -1217.93) * mm});
            skLineSegment(sketch, "E213.MirrorCS", {"start": v(-940.94, -1217.93) * mm, "end": v(-940.94, -1322.07) * mm});
            skLineSegment(sketch, "E214.MirrorCS", {"start": v(-915.54, -1217.93) * mm, "end": v(-915.54, -1322.07) * mm});
            skLineSegment(sketch, "E215.bottom", {"start": v(-593.72, -1217.93) * mm, "end": v(-619.12, -1217.93) * mm});
            skLineSegment(sketch, "E215.top", {"start": v(-593.72, -1322.07) * mm, "end": v(-619.12, -1322.07) * mm});
            skLineSegment(sketch, "E215.left", {"start": v(-593.72, -1217.93) * mm, "end": v(-593.72, -1322.07) * mm});
            skLineSegment(sketch, "E215.right", {"start": v(-619.12, -1217.93) * mm, "end": v(-619.12, -1322.07) * mm});
            skLineSegment(sketch, "E216.bottom", {"start": v(-593.72, -1398.27) * mm, "end": v(-611.76, -1398.27) * mm});
            skLineSegment(sketch, "E216.top", {"start": v(-593.72, -1322.07) * mm, "end": v(-611.76, -1322.07) * mm});
            skLineSegment(sketch, "E216.left", {"start": v(-593.72, -1398.27) * mm, "end": v(-593.72, -1322.07) * mm});
            skLineSegment(sketch, "E216.right", {"start": v(-611.76, -1398.27) * mm, "end": v(-611.76, -1322.07) * mm});
            skLineSegment(sketch, "E217.bottom", {"start": v(-441.32, -928.37) * mm, "end": v(-415.92, -928.37) * mm});
            skLineSegment(sketch, "E217.top", {"start": v(-441.32, -1791.97) * mm, "end": v(-415.92, -1791.97) * mm});
            skLineSegment(sketch, "E217.left", {"start": v(-441.32, -928.37) * mm, "end": v(-441.32, -1791.97) * mm});
            skLineSegment(sketch, "E217.right", {"start": v(-415.92, -928.37) * mm, "end": v(-415.92, -1791.97) * mm});
            skLineSegment(sketch, "E218.bottom", {"start": v(-940.94, -1398.27) * mm, "end": v(-922.9, -1398.27) * mm});
            skLineSegment(sketch, "E218.top", {"start": v(-940.94, -1322.07) * mm, "end": v(-922.9, -1322.07) * mm});
            skLineSegment(sketch, "E218.left", {"start": v(-940.94, -1398.27) * mm, "end": v(-940.94, -1322.07) * mm});
            skLineSegment(sketch, "E218.right", {"start": v(-922.9, -1398.27) * mm, "end": v(-922.9, -1322.07) * mm});
            skLineSegment(sketch, "E219.bottom", {"start": v(-940.94, -1791.97) * mm, "end": v(-922.9, -1791.97) * mm});
            skLineSegment(sketch, "E219.top", {"start": v(-940.94, -1715.77) * mm, "end": v(-922.9, -1715.77) * mm});
            skLineSegment(sketch, "E219.left", {"start": v(-940.94, -1791.97) * mm, "end": v(-940.94, -1715.77) * mm});
            skLineSegment(sketch, "E219.right", {"start": v(-922.9, -1791.97) * mm, "end": v(-922.9, -1715.77) * mm});
            skLineSegment(sketch, "E220.MirrorCS", {"start": v(-593.72, -1791.97) * mm, "end": v(-611.76, -1791.97) * mm});
            skLineSegment(sketch, "E221.MirrorCS", {"start": v(-593.72, -1791.97) * mm, "end": v(-593.72, -1715.77) * mm});
            skLineSegment(sketch, "E222.MirrorCS", {"start": v(-593.72, -1715.77) * mm, "end": v(-611.76, -1715.77) * mm});
            skLineSegment(sketch, "E223.MirrorCS", {"start": v(-611.76, -1791.97) * mm, "end": v(-611.76, -1715.77) * mm});
            skLineSegment(sketch, "E224", {"start": v(-441.32, -928.37) * mm, "end": v(-491.1, -928.37) * mm});
            skLineSegment(sketch, "E225", {"start": v(-491.1, -928.37) * mm, "end": v(-491.1, -1004.57) * mm});
            skLineSegment(sketch, "E226", {"start": v(-491.1, -1004.57) * mm, "end": v(-441.32, -1004.57) * mm});
            skLineSegment(sketch, "E227", {"start": v(-441.32, -1322.07) * mm, "end": v(-491.1, -1322.07) * mm});
            skLineSegment(sketch, "E228", {"start": v(-491.1, -1322.07) * mm, "end": v(-491.1, -1398.27) * mm});
            skLineSegment(sketch, "E229", {"start": v(-491.1, -1398.27) * mm, "end": v(-441.32, -1398.27) * mm});
            skLineSegment(sketch, "E230", {"start": v(-441.32, -1791.97) * mm, "end": v(-491.1, -1791.97) * mm});
            skLineSegment(sketch, "E231", {"start": v(-491.1, -1791.97) * mm, "end": v(-491.1, -1715.77) * mm});
            skLineSegment(sketch, "E232", {"start": v(-491.1, -1715.77) * mm, "end": v(-441.32, -1715.77) * mm});
            skLineSegment(sketch, "E233.MirrorCS", {"start": v(-776.35, -711.2) * mm, "end": v(-758.32, -711.2) * mm});
            skLineSegment(sketch, "E234.MirrorCS", {"start": v(-776.35, -711.2) * mm, "end": v(-776.35, -729.23) * mm});
            skLineSegment(sketch, "E235.MirrorCS", {"start": v(-827.15, -711.2) * mm, "end": v(-827.15, -729.23) * mm});
            skLineSegment(sketch, "E236.MirrorCS", {"start": v(-707.52, -711.2) * mm, "end": v(-707.52, -729.23) * mm});
            skLineSegment(sketch, "E237.MirrorCS", {"start": v(-758.32, -711.2) * mm, "end": v(-758.32, -729.23) * mm});
            skLineSegment(sketch, "E238.MirrorCS", {"start": v(-758.32, -729.23) * mm, "end": v(-707.52, -729.23) * mm});
            skLineSegment(sketch, "E239.MirrorCS", {"start": v(-776.35, -787.4) * mm, "end": v(-776.35, -711.2) * mm});
            skLineSegment(sketch, "E240.MirrorCS", {"start": v(-776.35, -729.23) * mm, "end": v(-827.15, -729.23) * mm});
            skLineSegment(sketch, "E241.MirrorCS", {"start": v(-776.35, -711.2) * mm, "end": v(-827.15, -711.2) * mm});
            skLineSegment(sketch, "E242.MirrorCS", {"start": v(-758.32, -711.2) * mm, "end": v(-707.52, -711.2) * mm});
            skLineSegment(sketch, "E243.MirrorCS", {"start": v(-758.32, -787.4) * mm, "end": v(-758.32, -711.2) * mm});
            skLineSegment(sketch, "E244.MirrorCS", {"start": v(-776.35, -787.4) * mm, "end": v(-758.32, -787.4) * mm});
            skLineSegment(sketch, "E245.MirrorCS", {"start": v(-758.32, -1828.8) * mm, "end": v(-758.32, -1810.77) * mm});
            skLineSegment(sketch, "E246.MirrorCS", {"start": v(-776.35, -1828.8) * mm, "end": v(-758.32, -1828.8) * mm});
            skLineSegment(sketch, "E247.MirrorCS", {"start": v(-776.35, -1828.8) * mm, "end": v(-776.35, -1810.77) * mm});
            skLineSegment(sketch, "E248.MirrorCS", {"start": v(-776.35, -1574.8) * mm, "end": v(-758.32, -1574.8) * mm});
            skLineSegment(sketch, "E249.MirrorCS", {"start": v(-776.35, -1752.6) * mm, "end": v(-758.32, -1752.6) * mm});
            skLineSegment(sketch, "E250.MirrorCS", {"start": v(-827.15, -1828.8) * mm, "end": v(-827.15, -1810.77) * mm});
            skLineSegment(sketch, "E251.MirrorCS", {"start": v(-758.32, -1828.8) * mm, "end": v(-758.32, -1752.6) * mm});
            skLineSegment(sketch, "E252.MirrorCS", {"start": v(-758.32, -1828.8) * mm, "end": v(-707.52, -1828.8) * mm});
            skLineSegment(sketch, "E253.MirrorCS", {"start": v(-758.32, -1810.77) * mm, "end": v(-707.52, -1810.77) * mm});
            skLineSegment(sketch, "E254.MirrorCS", {"start": v(-776.35, -1358.9) * mm, "end": v(-758.32, -1358.9) * mm});
            skLineSegment(sketch, "E255.MirrorCS", {"start": v(-707.52, -1828.8) * mm, "end": v(-707.52, -1810.77) * mm});
            skLineSegment(sketch, "E256.MirrorCS", {"start": v(-776.35, -1181.1) * mm, "end": v(-758.32, -1181.1) * mm});
            skLineSegment(sketch, "E257.MirrorCS", {"start": v(-776.35, -1828.8) * mm, "end": v(-776.35, -1752.6) * mm});
            skLineSegment(sketch, "E258.MirrorCS", {"start": v(-776.35, -1828.8) * mm, "end": v(-827.15, -1828.8) * mm});
            skLineSegment(sketch, "E259.MirrorCS", {"start": v(-776.35, -965.2) * mm, "end": v(-758.32, -965.2) * mm});
            skLineSegment(sketch, "E260.MirrorCS", {"start": v(-776.35, -1810.77) * mm, "end": v(-827.15, -1810.77) * mm});
            skPoint(sketch, "E261.MirrorP", {"position": v(-758.32, -1663.7) * mm});
            skLineSegment(sketch, "E262.MirrorCS", {"start": v(-776.35, -1574.8) * mm, "end": v(-776.35, -1358.9) * mm});
            skLineSegment(sketch, "E263.MirrorCS", {"start": v(-758.32, -1574.8) * mm, "end": v(-758.32, -1358.9) * mm});
            skLineSegment(sketch, "E264.MirrorCS", {"start": v(-758.32, -1181.1) * mm, "end": v(-758.32, -965.2) * mm});
            skLineSegment(sketch, "E265.MirrorCS", {"start": v(-776.35, -1181.1) * mm, "end": v(-776.35, -965.2) * mm});
            skLineSegment(sketch, "E266.MirrorCS", {"start": v(-758.32, -1752.6) * mm, "end": v(-758.32, -1574.8) * mm, "construction": true});
            skPoint(sketch, "E267.MirrorP", {"position": v(-767.33, -1828.8) * mm});
            skLineSegment(sketch, "E268", {"start": v(-1001.27, -558.8) * mm, "end": v(-1001.27, 558.8) * mm, "construction": true});
            skLineSegment(sketch, "E269.MirrorCS", {"start": v(-1226.18, 558.8) * mm, "end": v(-1226.18, 540.77) * mm});
            skLineSegment(sketch, "E270.MirrorCS", {"start": v(-1226.18, 558.8) * mm, "end": v(-1226.18, 482.6) * mm});
            skLineSegment(sketch, "E271.MirrorCS", {"start": v(-1226.18, 540.77) * mm, "end": v(-1175.38, 540.77) * mm});
            skLineSegment(sketch, "E272.MirrorCS", {"start": v(-1175.38, 558.8) * mm, "end": v(-1175.38, 540.77) * mm});
            skPoint(sketch, "E273.MirrorP", {"position": v(-1235.2, 558.8) * mm});
            skLineSegment(sketch, "E274.MirrorCS", {"start": v(-1226.18, 558.8) * mm, "end": v(-1175.38, 558.8) * mm});
            skLineSegment(sketch, "E275.MirrorCS", {"start": v(-1244.22, 558.8) * mm, "end": v(-1244.22, 482.6) * mm});
            skLineSegment(sketch, "E276.MirrorCS", {"start": v(-1226.18, 482.6) * mm, "end": v(-1244.22, 482.6) * mm});
            skLineSegment(sketch, "E277.MirrorCS", {"start": v(-1226.18, 558.8) * mm, "end": v(-1244.22, 558.8) * mm});
            skLineSegment(sketch, "E278.MirrorCS", {"start": v(-1244.22, 304.8) * mm, "end": v(-1244.22, 88.9) * mm});
            skLineSegment(sketch, "E279.MirrorCS", {"start": v(-1226.18, 304.8) * mm, "end": v(-1226.18, 88.9) * mm});
            skLineSegment(sketch, "E280.MirrorCS", {"start": v(-1226.18, 88.9) * mm, "end": v(-1244.22, 88.9) * mm});
            skLineSegment(sketch, "E281.MirrorCS", {"start": v(-1226.18, 304.8) * mm, "end": v(-1244.22, 304.8) * mm});
            skLineSegment(sketch, "E282.MirrorCS", {"start": v(-1226.18, -88.9) * mm, "end": v(-1244.22, -88.9) * mm});
            skLineSegment(sketch, "E283.MirrorCS", {"start": v(-1226.18, -558.8) * mm, "end": v(-1175.38, -558.8) * mm});
            skPoint(sketch, "E284.MirrorP", {"position": v(-1235.2, -558.8) * mm});
            skLineSegment(sketch, "E285.MirrorCS", {"start": v(-1226.18, -558.8) * mm, "end": v(-1226.18, -540.77) * mm});
            skLineSegment(sketch, "E286.MirrorCS", {"start": v(-1226.18, -540.77) * mm, "end": v(-1175.38, -540.77) * mm});
            skLineSegment(sketch, "E287.MirrorCS", {"start": v(-1175.38, -558.8) * mm, "end": v(-1175.38, -540.77) * mm});
            skLineSegment(sketch, "E288.MirrorCS", {"start": v(-1226.18, -558.8) * mm, "end": v(-1244.22, -558.8) * mm});
            skLineSegment(sketch, "E289.MirrorCS", {"start": v(-1226.18, -482.6) * mm, "end": v(-1226.18, -558.8) * mm});
            skLineSegment(sketch, "E290.MirrorCS", {"start": v(-1226.18, -482.6) * mm, "end": v(-1244.22, -482.6) * mm});
            skLineSegment(sketch, "E291.MirrorCS", {"start": v(-1244.22, -482.6) * mm, "end": v(-1244.22, -558.8) * mm});
            skLineSegment(sketch, "E292.MirrorCS", {"start": v(-1226.18, -88.9) * mm, "end": v(-1226.18, -304.8) * mm});
            skLineSegment(sketch, "E293.MirrorCS", {"start": v(-1244.22, -88.9) * mm, "end": v(-1244.22, -304.8) * mm});
            skLineSegment(sketch, "E294.MirrorCS", {"start": v(-1226.18, -304.8) * mm, "end": v(-1244.22, -304.8) * mm});
            skLineSegment(sketch, "E295", {"start": v(-1086.48, 558.8) * mm, "end": v(-1086.48, -558.8) * mm});
            skLineSegment(sketch, "E296", {"start": v(-1086.48, 558.8) * mm, "end": v(-1244.22, 558.8) * mm});
            skLineSegment(sketch, "E297", {"start": v(-1244.22, -558.8) * mm, "end": v(-1086.48, -558.8) * mm});
            skLineSegment(sketch, "E298", {"start": v(-1244.22, -558.8) * mm, "end": v(-1244.22, 558.8) * mm});
            skLineSegment(sketch, "E299.MirrorCS", {"start": v(-1226.18, -711.2) * mm, "end": v(-1244.22, -711.2) * mm});
            skLineSegment(sketch, "E300.MirrorCS", {"start": v(-1226.18, -711.2) * mm, "end": v(-1226.18, -729.23) * mm});
            skLineSegment(sketch, "E301.MirrorCS", {"start": v(-1226.18, -1828.8) * mm, "end": v(-1244.22, -1828.8) * mm});
            skLineSegment(sketch, "E302.MirrorCS", {"start": v(-1226.18, -1828.8) * mm, "end": v(-1226.18, -1810.77) * mm});
            skLineSegment(sketch, "E303.MirrorCS", {"start": v(-1226.18, -711.2) * mm, "end": v(-1175.38, -711.2) * mm});
            skLineSegment(sketch, "E304.MirrorCS", {"start": v(-1226.18, -787.4) * mm, "end": v(-1226.18, -711.2) * mm});
            skLineSegment(sketch, "E305.MirrorCS", {"start": v(-1175.38, -711.2) * mm, "end": v(-1175.38, -729.23) * mm});
            skLineSegment(sketch, "E306.MirrorCS", {"start": v(-1226.18, -729.23) * mm, "end": v(-1175.38, -729.23) * mm});
            skLineSegment(sketch, "E307.MirrorCS", {"start": v(-1226.18, -1828.8) * mm, "end": v(-1175.38, -1828.8) * mm});
            skLineSegment(sketch, "E308.MirrorCS", {"start": v(-1244.22, -787.4) * mm, "end": v(-1244.22, -711.2) * mm});
            skLineSegment(sketch, "E309.MirrorCS", {"start": v(-1175.38, -1828.8) * mm, "end": v(-1175.38, -1810.77) * mm});
            skLineSegment(sketch, "E310.MirrorCS", {"start": v(-1226.18, -787.4) * mm, "end": v(-1244.22, -787.4) * mm});
            skLineSegment(sketch, "E311.MirrorCS", {"start": v(-1226.18, -1810.77) * mm, "end": v(-1175.38, -1810.77) * mm});
            skLineSegment(sketch, "E312.MirrorCS", {"start": v(-1226.18, -1828.8) * mm, "end": v(-1226.18, -1752.6) * mm});
            skLineSegment(sketch, "E313.MirrorCS", {"start": v(-1226.18, -965.2) * mm, "end": v(-1244.22, -965.2) * mm});
            skLineSegment(sketch, "E314.MirrorCS", {"start": v(-1226.18, -1181.1) * mm, "end": v(-1244.22, -1181.1) * mm});
            skLineSegment(sketch, "E315.MirrorCS", {"start": v(-1226.18, -1752.6) * mm, "end": v(-1244.22, -1752.6) * mm});
            skLineSegment(sketch, "E316.MirrorCS", {"start": v(-1226.18, -1574.8) * mm, "end": v(-1244.22, -1574.8) * mm});
            skLineSegment(sketch, "E317.MirrorCS", {"start": v(-1244.22, -711.2) * mm, "end": v(-1086.48, -711.2) * mm});
            skLineSegment(sketch, "E318.MirrorCS", {"start": v(-1226.18, -1358.9) * mm, "end": v(-1244.22, -1358.9) * mm});
            skLineSegment(sketch, "E319.MirrorCS", {"start": v(-1086.48, -1828.8) * mm, "end": v(-1244.22, -1828.8) * mm});
            skLineSegment(sketch, "E320.MirrorCS", {"start": v(-1244.22, -1828.8) * mm, "end": v(-1244.22, -1752.6) * mm});
            skLineSegment(sketch, "E321.MirrorCS", {"start": v(-1244.22, -1574.8) * mm, "end": v(-1244.22, -1358.9) * mm});
            skLineSegment(sketch, "E322.MirrorCS", {"start": v(-1086.48, -1828.8) * mm, "end": v(-1086.48, -711.2) * mm});
            skPoint(sketch, "E323.MirrorP", {"position": v(-1235.2, -711.2) * mm});
            skPoint(sketch, "E324.MirrorP", {"position": v(-1235.2, -1828.8) * mm});
            skLineSegment(sketch, "E325.MirrorCS", {"start": v(-1244.22, -1181.1) * mm, "end": v(-1244.22, -965.2) * mm});
            skLineSegment(sketch, "E326.MirrorCS", {"start": v(-1244.22, -711.2) * mm, "end": v(-1244.22, -1828.8) * mm});
            skLineSegment(sketch, "E327.MirrorCS", {"start": v(-1226.18, -1574.8) * mm, "end": v(-1226.18, -1358.9) * mm});
            skLineSegment(sketch, "E328.MirrorCS", {"start": v(-1226.18, -1181.1) * mm, "end": v(-1226.18, -965.2) * mm});
            skLineSegment(sketch, "E329.bottom", {"start": v(-1086.48, -824.23) * mm, "end": v(-1061.08, -824.23) * mm});
            skLineSegment(sketch, "E329.top", {"start": v(-1086.48, -928.37) * mm, "end": v(-1061.08, -928.37) * mm});
            skLineSegment(sketch, "E329.left", {"start": v(-1086.48, -824.23) * mm, "end": v(-1086.48, -928.37) * mm});
            skLineSegment(sketch, "E329.right", {"start": v(-1061.08, -824.23) * mm, "end": v(-1061.08, -928.37) * mm});
            skPoint(sketch, "E330.firstSnap0", {"position": v(-1086.48, -1270) * mm});
            skLineSegment(sketch, "E330.bottom", {"start": v(-1086.48, -1322.07) * mm, "end": v(-1061.08, -1322.07) * mm});
            skLineSegment(sketch, "E330.top", {"start": v(-1086.48, -1217.93) * mm, "end": v(-1061.08, -1217.93) * mm});
            skLineSegment(sketch, "E330.left", {"start": v(-1086.48, -1322.07) * mm, "end": v(-1086.48, -1217.93) * mm});
            skLineSegment(sketch, "E330.right", {"start": v(-1061.08, -1322.07) * mm, "end": v(-1061.08, -1217.93) * mm});
            skLineSegment(sketch, "E331.bottom", {"start": v(-1086.48, -1715.77) * mm, "end": v(-1061.08, -1715.77) * mm});
            skLineSegment(sketch, "E331.top", {"start": v(-1086.48, -1611.63) * mm, "end": v(-1061.08, -1611.63) * mm});
            skLineSegment(sketch, "E331.left", {"start": v(-1086.48, -1715.77) * mm, "end": v(-1086.48, -1611.63) * mm});
            skLineSegment(sketch, "E331.right", {"start": v(-1061.08, -1715.77) * mm, "end": v(-1061.08, -1611.63) * mm});
            skLineSegment(sketch, "E332.bottom", {"start": v(-1086.48, -445.77) * mm, "end": v(-1130.2, -445.77) * mm});
            skLineSegment(sketch, "E332.top", {"start": v(-1086.48, -341.63) * mm, "end": v(-1130.2, -341.63) * mm});
            skLineSegment(sketch, "E332.left", {"start": v(-1086.48, -445.77) * mm, "end": v(-1086.48, -341.63) * mm});
            skLineSegment(sketch, "E332.right", {"start": v(-1130.2, -445.77) * mm, "end": v(-1130.2, -341.63) * mm});
            skLineSegment(sketch, "E333.bottom", {"start": v(-1086.48, -52.07) * mm, "end": v(-1130.2, -52.07) * mm});
            skLineSegment(sketch, "E333.top", {"start": v(-1086.48, 52.07) * mm, "end": v(-1130.2, 52.07) * mm});
            skLineSegment(sketch, "E333.left", {"start": v(-1086.48, -52.07) * mm, "end": v(-1086.48, 52.07) * mm});
            skLineSegment(sketch, "E333.right", {"start": v(-1130.2, -52.07) * mm, "end": v(-1130.2, 52.07) * mm});
            skLineSegment(sketch, "E334.bottom", {"start": v(-1086.48, 341.63) * mm, "end": v(-1130.2, 341.63) * mm});
            skLineSegment(sketch, "E334.top", {"start": v(-1086.48, 445.77) * mm, "end": v(-1130.2, 445.77) * mm});
            skLineSegment(sketch, "E334.left", {"start": v(-1086.48, 341.63) * mm, "end": v(-1086.48, 445.77) * mm});
            skLineSegment(sketch, "E334.right", {"start": v(-1130.2, 341.63) * mm, "end": v(-1130.2, 445.77) * mm});
            skLineSegment(sketch, "E335", {"start": v(-439.17, 1345.82) * mm, "end": v(-439.17, 1188.08) * mm});
            skLineSegment(sketch, "E336", {"start": v(-439.17, 1188.08) * mm, "end": v(439.17, 1188.08) * mm});
            skLineSegment(sketch, "E337", {"start": v(439.17, 1188.08) * mm, "end": v(439.17, 1345.82) * mm});
            skSolve(sketch);
        }
        {
            var Q0;
            {var subQ1=sQuery(id+"F1.wireOp",EDGE,"E60.bottom");Q0=makeQuery(id+"F1.imprint","IMPRINT",FACE,{"disambiguationData":[TD([[makeQuery(id+"F1.imprint","IMPRINT",EDGE,{"derivedFrom":subQ1}),-1.0]])]});}
            var Q1;
            Q1=makeQuery(id+"F1.imprint","IMPRINT",FACE,{"disambiguationData":[TD([[makeQuery(id+"F1.imprint","IMPRINT",EDGE,{"derivedFrom":sQuery(id+"F1.wireOp",EDGE,"E61.bottom")}),-1.0]])]});
            var Q2;
            Q2=makeQuery(id+"F1.imprint","IMPRINT",FACE,{"disambiguationData":[TD([[makeQuery(id+"F1.imprint","IMPRINT",EDGE,{"derivedFrom":sQuery(id+"F1.wireOp",EDGE,"E62.bottom")}),1.0]])]});
            var Q3;
            Q3=makeQuery(id+"F1.imprint","IMPRINT",FACE,{"disambiguationData":[TD([[makeQuery(id+"F1.imprint","IMPRINT",EDGE,{"derivedFrom":sQuery(id+"F1.wireOp",EDGE,"E70.MirrorCS")}),1.0]])]});
            var Q4;
            Q4=makeQuery(id+"F1.imprint","IMPRINT",FACE,{"disambiguationData":[TD([[makeQuery(id+"F1.imprint","IMPRINT",EDGE,{"derivedFrom":sQuery(id+"F1.wireOp",EDGE,"E74.MirrorCS")}),1.0]])]});
            var Q5;
            {var subQ33=sQuery(id+"F1.wireOp",EDGE,"E1.bottom");Q5=makeQuery(id+"F1.imprint","IMPRINT",FACE,{"disambiguationData":[TD([[makeQuery(id+"F1.imprint","IMPRINT",EDGE,{"derivedFrom":subQ33}),1.0]])]});}
            var Q6;
            {var subQ6=sQuery(id+"F1.wireOp",EDGE,"E43.left");Q6=makeQuery(id+"F1.imprint","IMPRINT",FACE,{"disambiguationData":[TD([[makeQuery(id+"F1.imprint","IMPRINT",EDGE,{"derivedFrom":subQ6}),1.0]])]});}
            var Q7;
            {var subQ3=sQuery(id+"F1.wireOp",EDGE,"15a585a5-c292-47de-8cfe-40bc0ff959e20.MirrorCS");Q7=makeQuery(id+"F1.imprint","IMPRINT",FACE,{"disambiguationData":[TD([[makeQuery(id+"F1.imprint","IMPRINT",EDGE,{"derivedFrom":subQ3}),1.0]])]});}
            var Q8;
            {var subQ0=sQuery(id+"F1.wireOp",EDGE,"E94.MirrorCS");Q8=makeQuery(id+"F1.imprint","IMPRINT",FACE,{"disambiguationData":[TD([[makeQuery(id+"F1.imprint","IMPRINT",EDGE,{"derivedFrom":subQ0}),1.0]])]});}
            var Q9;
            {var subQ0=sQuery(id+"F1.wireOp",EDGE,"E100.MirrorCS");Q9=makeQuery(id+"F1.imprint","IMPRINT",FACE,{"disambiguationData":[TD([[makeQuery(id+"F1.imprint","IMPRINT",EDGE,{"derivedFrom":subQ0}),-1.0]])]});}
            var Q10;
            {var subQ10=sQuery(id+"F1.wireOp",EDGE,"E173.bottom");Q10=makeQuery(id+"F1.imprint","IMPRINT",FACE,{"disambiguationData":[TD([[makeQuery(id+"F1.imprint","IMPRINT",EDGE,{"derivedFrom":subQ10}),-1.0]])]});}
            var Q11;
            {var subQ0=sQuery(id+"F1.wireOp",EDGE,"vC60dyBu-nMOn-iXCW-ycnC-LK4FzoJF3nVa");Q11=makeQuery(id+"F1.imprint","IMPRINT",FACE,{"disambiguationData":[TD([[makeQuery(id+"F1.imprint","IMPRINT",EDGE,{"derivedFrom":subQ0}),-1.0]])]});}
            var Q12;
            {var subQ0=sQuery(id+"F1.wireOp",EDGE,"E227");Q12=makeQuery(id+"F1.imprint","IMPRINT",FACE,{"disambiguationData":[TD([[makeQuery(id+"F1.imprint","IMPRINT",EDGE,{"derivedFrom":subQ0}),1.0]])]});}
            var Q13;
            {var subQ0=sQuery(id+"F1.wireOp",EDGE,"E230");Q13=makeQuery(id+"F1.imprint","IMPRINT",FACE,{"disambiguationData":[TD([[makeQuery(id+"F1.imprint","IMPRINT",EDGE,{"derivedFrom":subQ0}),-1.0]])]});}
            var Q14;
            {var subQ3=sQuery(id+"F1.wireOp",EDGE,"E217.bottom");Q14=makeQuery(id+"F1.imprint","IMPRINT",FACE,{"disambiguationData":[TD([[makeQuery(id+"F1.imprint","IMPRINT",EDGE,{"derivedFrom":subQ3}),-1.0]])]});}
            var Q15;
            {var subQ0=sQuery(id+"F1.wireOp",EDGE,"E224");Q15=makeQuery(id+"F1.imprint","IMPRINT",FACE,{"disambiguationData":[TD([[makeQuery(id+"F1.imprint","IMPRINT",EDGE,{"derivedFrom":subQ0}),1.0]])]});}
            var Q16;
            {var subQ26=sQuery(id+"F1.wireOp",EDGE,"E271.MirrorCS");Q16=makeQuery(id+"F1.imprint","IMPRINT",FACE,{"disambiguationData":[TD([[makeQuery(id+"F1.imprint","IMPRINT",EDGE,{"derivedFrom":subQ26}),-1.0]])]});}
            var Q17;
            Q17=makeQuery(id+"F1.imprint","IMPRINT",FACE,{"disambiguationData":[TD([[makeQuery(id+"F1.imprint","IMPRINT",EDGE,{"derivedFrom":sQuery(id+"F1.wireOp",EDGE,"E329.bottom")}),-1.0]])]});
            var Q18;
            Q18=makeQuery(id+"F1.imprint","IMPRINT",FACE,{"disambiguationData":[TD([[makeQuery(id+"F1.imprint","IMPRINT",EDGE,{"derivedFrom":sQuery(id+"F1.wireOp",EDGE,"E331.bottom")}),1.0]])]});
            var Q19;
            Q19=makeQuery(id+"F1.imprint","IMPRINT",FACE,{"disambiguationData":[TD([[makeQuery(id+"F1.imprint","IMPRINT",EDGE,{"derivedFrom":sQuery(id+"F1.wireOp",EDGE,"E330.bottom")}),1.0]])]});
            var Q20;
            {var subQ15=sQuery(id+"F1.wireOp",EDGE,"E305.MirrorCS");Q20=makeQuery(id+"F1.imprint","IMPRINT",FACE,{"disambiguationData":[TD([[makeQuery(id+"F1.imprint","IMPRINT",EDGE,{"derivedFrom":subQ15}),1.0]])]});}
            var Q21;
            Q21=makeQuery(id+"F1.imprint","IMPRINT",FACE,{"disambiguationData":[TD([[makeQuery(id+"F1.imprint","IMPRINT",EDGE,{"derivedFrom":sQuery(id+"F1.wireOp",EDGE,"E86.MirrorCS")}),-1.0]])]});
            extrude(context, id + "F2", {"entities" : qUnion([Q0, Q1, Q2, Q3, Q4, Q5, Q6, Q7, Q8, Q9, Q10, Q11, Q12, Q13, Q14, Q15, Q16, Q17, Q18, Q19, Q20, Q21]), "depth" : (getVariable(context, 'ply34')) * mm});
        }
        {
            var Q0;
            {var subQ6=sQuery(id+"F1.wireOp",EDGE,"E157.bottom");Q0=makeQuery(id+"F1.imprint","IMPRINT",FACE,{"disambiguationData":[TD([[makeQuery(id+"F1.imprint","IMPRINT",EDGE,{"derivedFrom":subQ6}),-1.0]])]});}
            var Q1;
            {var subQ0=sQuery(id+"F1.wireOp",EDGE,"E163");Q1=makeQuery(id+"F1.imprint","IMPRINT",FACE,{"disambiguationData":[TD([[makeQuery(id+"F1.imprint","IMPRINT",EDGE,{"derivedFrom":subQ0}),-1.0]])]});}
            var Q2;
            {var subQ0=sQuery(id+"F1.wireOp",EDGE,"E160");Q2=makeQuery(id+"F1.imprint","IMPRINT",FACE,{"disambiguationData":[TD([[makeQuery(id+"F1.imprint","IMPRINT",EDGE,{"derivedFrom":subQ0}),-1.0]])]});}
            var Q3;
            {var subQ0=sQuery(id+"F1.wireOp",EDGE,"E166");Q3=makeQuery(id+"F1.imprint","IMPRINT",FACE,{"disambiguationData":[TD([[makeQuery(id+"F1.imprint","IMPRINT",EDGE,{"derivedFrom":subQ0}),-1.0]])]});}
            var Q4;
            {var subQ0=sQuery(id+"F1.wireOp",EDGE,"E169");Q4=makeQuery(id+"F1.imprint","IMPRINT",FACE,{"disambiguationData":[TD([[makeQuery(id+"F1.imprint","IMPRINT",EDGE,{"derivedFrom":subQ0}),-1.0]])]});}
            extrude(context, id + "F3", {"entities" : qUnion([Q0, Q1, Q2, Q3, Q4]), "depth" : 12.2 * mm});
        }
        {
            var Q0;
            Q0=makeQuery(id+"F1.imprint","IMPRINT",FACE,{"disambiguationData":[TD([[makeQuery(id+"F1.imprint","IMPRINT",EDGE,{"derivedFrom":sQuery(id+"F1.wireOp",EDGE,"c5a33fef-cf20-4e9f-8e37-3778fd242a644.MirrorCS")}),1.0]])]});
            var Q1;
            Q1=makeQuery(id+"F1.imprint","IMPRINT",FACE,{"disambiguationData":[TD([[makeQuery(id+"F1.imprint","IMPRINT",EDGE,{"derivedFrom":sQuery(id+"F1.wireOp",EDGE,"E120.MirrorCS")}),1.0]])]});
            var Q2;
            Q2=makeQuery(id+"F1.imprint","IMPRINT",FACE,{"disambiguationData":[TD([[makeQuery(id+"F1.imprint","IMPRINT",EDGE,{"derivedFrom":sQuery(id+"F1.wireOp",EDGE,"E112.bottom")}),1.0]])]});
            var Q3;
            Q3=makeQuery(id+"F1.imprint","IMPRINT",FACE,{"disambiguationData":[TD([[makeQuery(id+"F1.imprint","IMPRINT",EDGE,{"derivedFrom":sQuery(id+"F1.wireOp",EDGE,"E109.bottom")}),1.0]])]});
            var Q4;
            Q4=makeQuery(id+"F1.imprint","IMPRINT",FACE,{"disambiguationData":[TD([[makeQuery(id+"F1.imprint","IMPRINT",EDGE,{"derivedFrom":sQuery(id+"F1.wireOp",EDGE,"E122.MirrorCS")}),1.0]])]});
            var Q5;
            Q5=makeQuery(id+"F1.imprint","IMPRINT",FACE,{"disambiguationData":[TD([[makeQuery(id+"F1.imprint","IMPRINT",EDGE,{"derivedFrom":sQuery(id+"F1.wireOp",EDGE,"c5a33fef-cf20-4e9f-8e37-3778fd242a642.MirrorCS")}),-1.0]])]});
            var Q6;
            Q6=makeQuery(id+"F1.imprint","IMPRINT",FACE,{"disambiguationData":[TD([[makeQuery(id+"F1.imprint","IMPRINT",EDGE,{"derivedFrom":sQuery(id+"F1.wireOp",EDGE,"c5a33fef-cf20-4e9f-8e37-3778fd242a640.MirrorCS")}),-1.0]])]});
            var Q7;
            Q7=makeQuery(id+"F1.imprint","IMPRINT",FACE,{"disambiguationData":[TD([[makeQuery(id+"F1.imprint","IMPRINT",EDGE,{"derivedFrom":sQuery(id+"F1.wireOp",EDGE,"E118.MirrorCS")}),-1.0]])]});
            var Q8;
            Q8=makeQuery(id+"F1.imprint","IMPRINT",FACE,{"disambiguationData":[TD([[makeQuery(id+"F1.imprint","IMPRINT",EDGE,{"derivedFrom":sQuery(id+"F1.wireOp",EDGE,"E113.MirrorCS")}),-1.0]])]});
            var Q9;
            Q9=makeQuery(id+"F1.imprint","IMPRINT",FACE,{"disambiguationData":[TD([[makeQuery(id+"F1.imprint","IMPRINT",EDGE,{"derivedFrom":sQuery(id+"F1.wireOp",EDGE,"E332.bottom")}),-1.0]])]});
            var Q10;
            Q10=makeQuery(id+"F1.imprint","IMPRINT",FACE,{"disambiguationData":[TD([[makeQuery(id+"F1.imprint","IMPRINT",EDGE,{"derivedFrom":sQuery(id+"F1.wireOp",EDGE,"E333.bottom")}),-1.0]])]});
            var Q11;
            Q11=makeQuery(id+"F1.imprint","IMPRINT",FACE,{"disambiguationData":[TD([[makeQuery(id+"F1.imprint","IMPRINT",EDGE,{"derivedFrom":sQuery(id+"F1.wireOp",EDGE,"E334.bottom")}),-1.0]])]});
            extrude(context, id + "F4", {"entities" : qUnion([Q0, Q1, Q2, Q3, Q4, Q5, Q6, Q7, Q8, Q9, Q10, Q11]), "operationType" : NewBodyOperationType.ADD, "depth" : (getVariable(context, 'ply34') - .129) * mm});
        }
    });
